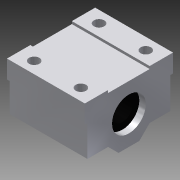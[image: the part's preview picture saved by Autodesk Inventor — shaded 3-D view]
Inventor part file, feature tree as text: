
AUTODESK INVENTOR PART (.ipt)
format: ipt  version: 2015 SP1 (Build 190203100, 203)  size: 143,360 bytes
history: native  units: mm
features: extrude x3, sketch x2, projected_geometry x2
ambient origin geometry x8: Origin, YZ Plane, XZ Plane, XY Plane, X Axis, Y Axis, Z Axis, Center Point
bodies: Solid1 (feature_tree)
feature tree (7):
  sketch  "Sketch1"  dims[d0=34.0mm d1=22.0mm]
  extrude  "Extrusion1"  Depth=22.0mm
  extrude  "Extrusion2"  Depth=6.0mm
  extrude  "Extrusion3"  Depth=18.0mm
  sketch  "Sketch2"  dims[d2=11.0mm d3=6.0mm d4=18.0mm d5=1.0mm d6=8.0mm d7=13.0mm d9=5.0mm d10=4.0mm d11=4.0mm d12=8.0mm d13=30.0mm d14=0.0mm d15=25.0mm d16=0.0mm d17=1.0mm d18=4.5mm d19=18.0mm d20=4.0mm d21=25.0mm d22=0.0mm]
  projected_geometry  "Projected Loop1"
  projected_geometry  "Projected Loop2"
